# Revit family: 202_FEV1-_
name_source: partatom
category: Air Terminals
revit_build: Autodesk Revit 2018 (Build: 20170223_1515(x64)
units: mm (PartAtom-declared; Revit-internal decimal feet)

## family parameters
Always vertical = Yes
Cut with Voids When Loaded = No
Part Type = Normal
Room Calculation Point = Yes
Round Connector Dimension = Use Diameter
Shared = No
Work Plane-Based = No

## types (3) — shared parameters
CAT0 = Yes
CL_Location_5000 = 5000 mm  [stored 16.4042 ft]
Description = Extract Valve
H1 = 20 mm  [stored 0.0656168 ft]
L_ARR = 400 mm  [stored 1.31234 ft]
Manufacturer = Flexit
QmdConnectorList = 201;D
W_ARR = 400 mm  [stored 1.31234 ft]
XRefLineVPlnId = 7453
Y3 = 50 mm  [stored 0.164042 ft]
YRefLineVPlnId = 7456
magiPartTypeId = 202
magiProductFamilyId = FEV1-*
zero-valued in all types: CLBTZ, H_ARR

## per-type parameters (varying)
| type | D | Y4 | magiProductId |
| 100-09703 | 100 mm | 73 mm | FEV1-100 |
| 125-09705 | 125 mm | 80 mm  [stored 0.262467 ft] | FEV1-125 |
| 160-02707 | 160 mm | 98 mm | FEV1-160 |

note: column(s) folded — value = type name in every type: MC Product Code

note: [stored X ft] marks values corroborated as IEEE doubles in the binary element streams (Revit-internal decimal feet)

## geometry (parser evidence)
native form markers: Sweep x1
no freeform markers — native parametric forms only
